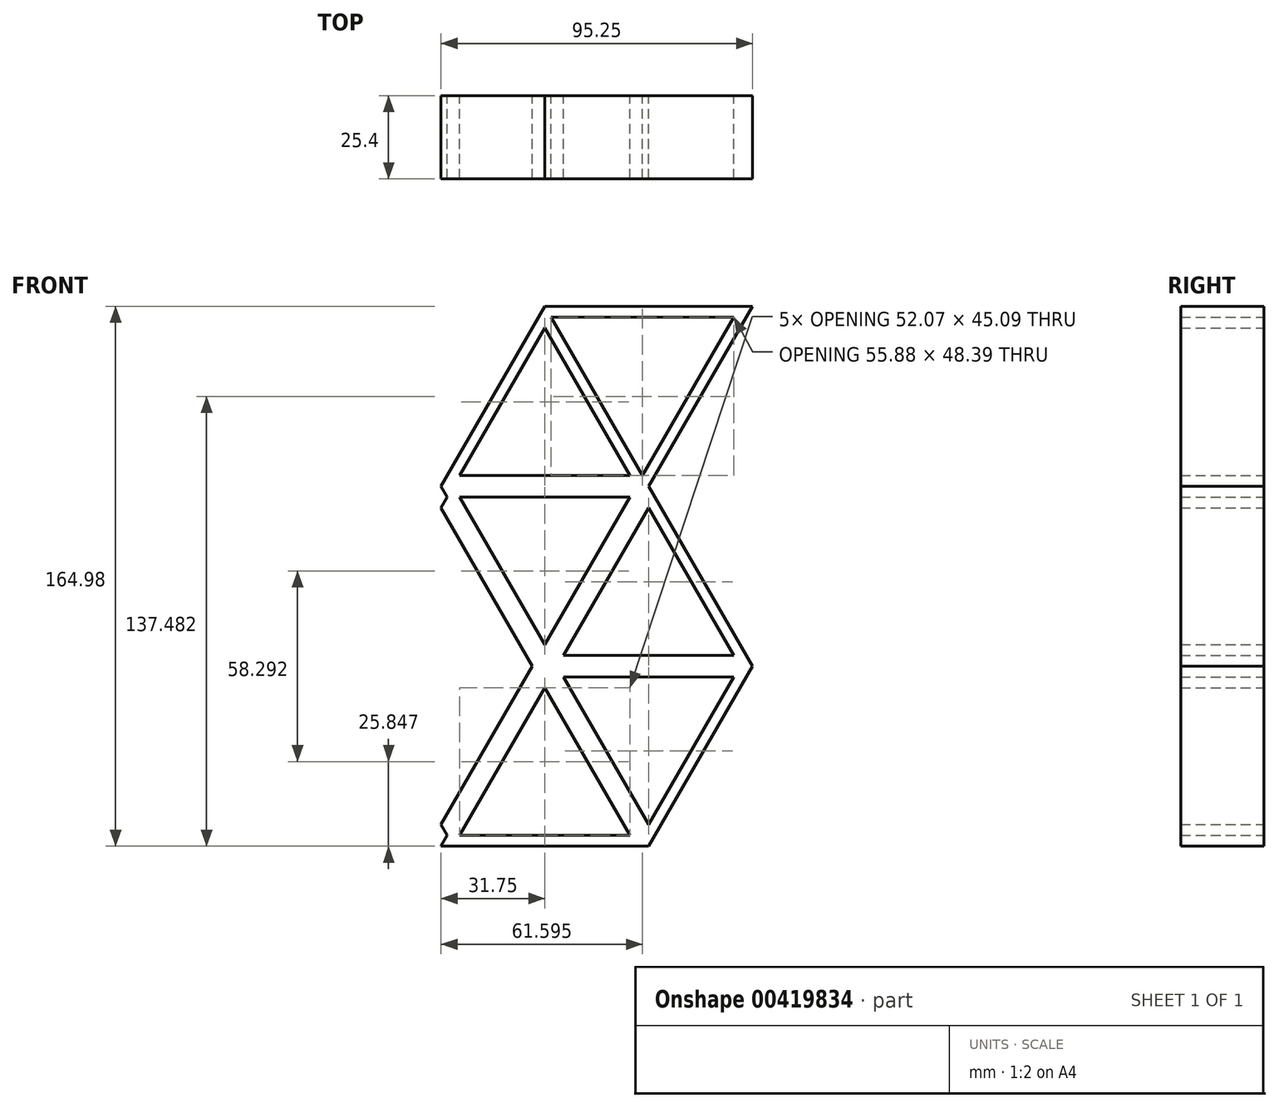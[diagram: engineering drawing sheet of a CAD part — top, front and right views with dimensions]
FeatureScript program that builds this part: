
annotation { "Feature Type Name" : "Feature", "Feature Type Description" : "" }
export const myFeature = defineFeature(function(context is Context, id is Id, definition is map)
    precondition{}
    {
        {
            var Q0;
            Q0=qCreatedBy(makeId("Front.planeOp"),FACE);
            var sketch = newSketch(context, id + "F0", { "sketchPlane" : qUnion([Q0])});
            skLineSegment(sketch, "E0", {"start": v(0, 0) * mm, "end": v(63.5, 0) * mm});
            skLineSegment(sketch, "E1", {"start": v(63.5, 0) * mm, "end": v(95.25, 55) * mm});
            skLineSegment(sketch, "E2", {"start": v(95.25, 55) * mm, "end": v(63.5, 109.99) * mm});
            skLineSegment(sketch, "E3", {"start": v(63.5, 109.99) * mm, "end": v(0, 109.99) * mm});
            skLineSegment(sketch, "E4", {"start": v(0, 109.99) * mm, "end": v(-31.75, 55) * mm});
            skLineSegment(sketch, "E5", {"start": v(-31.75, 55) * mm, "end": v(0, 0) * mm});
            skLineSegment(sketch, "E6", {"start": v(-31.75, 55) * mm, "end": v(95.25, 55) * mm});
            skLineSegment(sketch, "E7", {"start": v(63.5, 0) * mm, "end": v(0, 109.99) * mm});
            skLineSegment(sketch, "E8", {"start": v(0, 0) * mm, "end": v(63.5, 109.99) * mm});
            skLineSegment(sketch, "E9", {"start": v(63.5, 109.99) * mm, "end": v(95.25, 164.98) * mm});
            skLineSegment(sketch, "E10", {"start": v(0, 109.99) * mm, "end": v(-31.75, 164.98) * mm});
            skLineSegment(sketch, "E11", {"start": v(-31.75, 164.98) * mm, "end": v(95.25, 164.98) * mm});
            skLineSegment(sketch, "E12", {"start": v(1.9, 3.3) * mm, "end": v(61.6, 3.3) * mm});
            skLineSegment(sketch, "E13", {"start": v(61.6, 3.3) * mm, "end": v(91.44, 55) * mm});
            skLineSegment(sketch, "E14", {"start": v(91.44, 55) * mm, "end": v(61.6, 106.69) * mm});
            skLineSegment(sketch, "E15", {"start": v(61.6, 106.69) * mm, "end": v(1.9, 106.69) * mm});
            skLineSegment(sketch, "E16", {"start": v(1.9, 106.69) * mm, "end": v(-27.94, 55) * mm});
            skLineSegment(sketch, "E17", {"start": v(-27.94, 55) * mm, "end": v(1.9, 3.3) * mm});
            skLineSegment(sketch, "E18", {"start": v(5.72, 3.3) * mm, "end": v(63.5, 103.39) * mm});
            skLineSegment(sketch, "E19", {"start": v(57.78, 3.3) * mm, "end": v(0, 103.39) * mm});
            skLineSegment(sketch, "E20", {"start": v(63.5, 6.6) * mm, "end": v(5.72, 106.69) * mm});
            skLineSegment(sketch, "E21", {"start": v(89.53, 51.7) * mm, "end": v(-26.03, 51.7) * mm});
            skLineSegment(sketch, "E22", {"start": v(89.53, 58.3) * mm, "end": v(-26.03, 58.3) * mm});
            skLineSegment(sketch, "E23", {"start": v(57.78, 106.69) * mm, "end": v(0, 6.6) * mm});
            skLineSegment(sketch, "E24", {"start": v(0, 109.99) * mm, "end": v(31.75, 164.98) * mm});
            skLineSegment(sketch, "E25", {"start": v(31.75, 164.98) * mm, "end": v(63.5, 109.99) * mm});
            skLineSegment(sketch, "E26", {"start": v(-27.94, 164.98) * mm, "end": v(1.9, 113.28) * mm});
            skLineSegment(sketch, "E27", {"start": v(1.9, 113.28) * mm, "end": v(61.6, 113.28) * mm});
            skLineSegment(sketch, "E28", {"start": v(61.6, 113.28) * mm, "end": v(91.44, 164.98) * mm});
            skLineSegment(sketch, "E29", {"start": v(-29.84, 161.68) * mm, "end": v(93.34, 161.68) * mm});
            skLineSegment(sketch, "E30", {"start": v(5.71, 113.28) * mm, "end": v(35.56, 164.98) * mm});
            skLineSegment(sketch, "E31", {"start": v(57.79, 113.28) * mm, "end": v(27.94, 164.98) * mm});
            skSolve(sketch);
        }
        {
            var Q0;
            {var subQ0=sQuery(id+"F0.wireOp",EDGE,"E28");var subQ1=sQuery(id+"F0.wireOp",EDGE,"E11");var subQ2=makeQuery(id+"F0.imprint","INTERSECT",VERTEX,{"derivedFrom":[subQ1,subQ0]});Q0=makeQuery(id+"F0.imprint","IMPRINT",FACE,{"disambiguationData":[TD([[makeQuery(id+"F0.imprint","IMPRINT",EDGE,{"disambiguationData":[TD([[subQ2,1.0]])],"derivedFrom":subQ1}),-1.0]])]});}
            var Q1;
            {var subQ0=sQuery(id+"F0.wireOp",EDGE,"E11");var subQ1=sQuery(id+"F0.wireOp",EDGE,"E9");var subQ2=makeQuery(id+"F0.imprint","INTERSECT",VERTEX,{"derivedFrom":[subQ1,subQ0]});Q1=makeQuery(id+"F0.imprint","IMPRINT",FACE,{"disambiguationData":[TD([[makeQuery(id+"F0.imprint","IMPRINT",EDGE,{"disambiguationData":[TD([[subQ2,1.0]])],"derivedFrom":subQ1}),1.0]])]});}
            var Q2;
            {var subQ1=sQuery(id+"F0.wireOp",EDGE,"E9");var subQ3=sQuery(id+"F0.wireOp",EDGE,"E29");var subQ4=makeQuery(id+"F0.imprint","INTERSECT",VERTEX,{"derivedFrom":[subQ1,subQ3]});Q2=makeQuery(id+"F0.imprint","IMPRINT",FACE,{"disambiguationData":[TD([[makeQuery(id+"F0.imprint","IMPRINT",EDGE,{"disambiguationData":[TD([[subQ4,1.0]])],"derivedFrom":subQ3}),-1.0]])]});}
            var Q3;
            {var subQ1=sQuery(id+"F0.wireOp",EDGE,"E11");var subQ3=sQuery(id+"F0.wireOp",EDGE,"E30");var subQ4=makeQuery(id+"F0.imprint","INTERSECT",VERTEX,{"derivedFrom":[subQ1,subQ3]});Q3=makeQuery(id+"F0.imprint","IMPRINT",FACE,{"disambiguationData":[TD([[makeQuery(id+"F0.imprint","IMPRINT",EDGE,{"disambiguationData":[TD([[subQ4,1.0]])],"derivedFrom":subQ1}),-1.0]])]});}
            var Q4;
            {var subQ0=sQuery(id+"F0.wireOp",EDGE,"E31");var subQ3=sQuery(id+"F0.wireOp",EDGE,"E30");var subQ5=makeQuery(id+"F0.imprint","INTERSECT",VERTEX,{"derivedFrom":[subQ3,subQ0]});Q4=makeQuery(id+"F0.imprint","IMPRINT",FACE,{"disambiguationData":[TD([[makeQuery(id+"F0.imprint","IMPRINT",EDGE,{"disambiguationData":[TD([[subQ5,-1.0]])],"derivedFrom":subQ3}),1.0]])]});}
            var Q5;
            {var subQ0=sQuery(id+"F0.wireOp",EDGE,"E25");var subQ1=sQuery(id+"F0.wireOp",EDGE,"E24");var subQ2=makeQuery(id+"F0.imprint","INTERSECT",VERTEX,{"derivedFrom":[sQuery(id+"F0.wireOp",EDGE,"E11"),subQ1,subQ0]});Q5=makeQuery(id+"F0.imprint","IMPRINT",FACE,{"disambiguationData":[TD([[makeQuery(id+"F0.imprint","IMPRINT",EDGE,{"disambiguationData":[TD([[subQ2,1.0]])],"derivedFrom":subQ1}),-1.0]])]});}
            var Q6;
            {var subQ0=sQuery(id+"F0.wireOp",EDGE,"E27");var subQ5=sQuery(id+"F0.wireOp",EDGE,"E31");var subQ7=makeQuery(id+"F0.imprint","INTERSECT",VERTEX,{"derivedFrom":[subQ0,subQ5]});Q6=makeQuery(id+"F0.imprint","IMPRINT",FACE,{"disambiguationData":[TD([[makeQuery(id+"F0.imprint","IMPRINT",EDGE,{"disambiguationData":[TD([[subQ7,-1.0]])],"derivedFrom":subQ5}),-1.0]])]});}
            var Q7;
            {var subQ0=sQuery(id+"F0.wireOp",EDGE,"E27");var subQ5=sQuery(id+"F0.wireOp",EDGE,"E30");var subQ6=makeQuery(id+"F0.imprint","INTERSECT",VERTEX,{"derivedFrom":[subQ0,subQ5]});Q7=makeQuery(id+"F0.imprint","IMPRINT",FACE,{"disambiguationData":[TD([[makeQuery(id+"F0.imprint","IMPRINT",EDGE,{"disambiguationData":[TD([[subQ6,-1.0]])],"derivedFrom":subQ5}),1.0]])]});}
            var Q8;
            {var subQ5=sQuery(id+"F0.wireOp",EDGE,"E3");Q8=makeQuery(id+"F0.imprint","IMPRINT",FACE,{"disambiguationData":[TD([[makeQuery(id+"F0.imprint","IMPRINT",EDGE,{"derivedFrom":subQ5}),-1.0]])]});}
            var Q9;
            {var subQ1=sQuery(id+"F0.wireOp",EDGE,"E3");Q9=makeQuery(id+"F0.imprint","IMPRINT",FACE,{"disambiguationData":[TD([[makeQuery(id+"F0.imprint","IMPRINT",EDGE,{"derivedFrom":subQ1}),1.0]])]});}
            var Q10;
            {var subQ0=sQuery(id+"F0.wireOp",EDGE,"E15");var subQ5=sQuery(id+"F0.wireOp",EDGE,"E20");var subQ6=makeQuery(id+"F0.imprint","INTERSECT",VERTEX,{"derivedFrom":[subQ0,subQ5]});Q10=makeQuery(id+"F0.imprint","IMPRINT",FACE,{"disambiguationData":[TD([[makeQuery(id+"F0.imprint","IMPRINT",EDGE,{"disambiguationData":[TD([[subQ6,1.0]])],"derivedFrom":subQ5}),1.0]])]});}
            var Q11;
            {var subQ0=sQuery(id+"F0.wireOp",EDGE,"E15");var subQ5=sQuery(id+"F0.wireOp",EDGE,"E23");var subQ6=makeQuery(id+"F0.imprint","INTERSECT",VERTEX,{"derivedFrom":[subQ0,subQ5]});Q11=makeQuery(id+"F0.imprint","IMPRINT",FACE,{"disambiguationData":[TD([[makeQuery(id+"F0.imprint","IMPRINT",EDGE,{"disambiguationData":[TD([[subQ6,-1.0]])],"derivedFrom":subQ5}),1.0]])]});}
            var Q12;
            {var subQ0=sQuery(id+"F0.wireOp",EDGE,"E23");var subQ1=sQuery(id+"F0.wireOp",EDGE,"E20");var subQ2=makeQuery(id+"F0.imprint","INTERSECT",VERTEX,{"derivedFrom":[subQ1,subQ0]});Q12=makeQuery(id+"F0.imprint","IMPRINT",FACE,{"disambiguationData":[TD([[makeQuery(id+"F0.imprint","IMPRINT",EDGE,{"disambiguationData":[TD([[subQ2,1.0]])],"derivedFrom":subQ1}),1.0]])]});}
            var Q13;
            {var subQ0=sQuery(id+"F0.wireOp",EDGE,"E8");var subQ1=sQuery(id+"F0.wireOp",EDGE,"E6");var subQ2=makeQuery(id+"F0.imprint","INTERSECT",VERTEX,{"derivedFrom":[subQ1,sQuery(id+"F0.wireOp",EDGE,"E7"),subQ0]});Q13=makeQuery(id+"F0.imprint","IMPRINT",FACE,{"disambiguationData":[TD([[makeQuery(id+"F0.imprint","IMPRINT",EDGE,{"disambiguationData":[TD([[subQ2,-1.0]])],"derivedFrom":subQ1}),1.0]])]});}
            var Q14;
            {var subQ0=sQuery(id+"F0.wireOp",EDGE,"E8");var subQ1=sQuery(id+"F0.wireOp",EDGE,"E7");var subQ2=makeQuery(id+"F0.imprint","INTERSECT",VERTEX,{"derivedFrom":[sQuery(id+"F0.wireOp",EDGE,"E6"),subQ1,subQ0]});Q14=makeQuery(id+"F0.imprint","IMPRINT",FACE,{"disambiguationData":[TD([[makeQuery(id+"F0.imprint","IMPRINT",EDGE,{"disambiguationData":[TD([[subQ2,-1.0]])],"derivedFrom":subQ1}),-1.0]])]});}
            var Q15;
            {var subQ0=sQuery(id+"F0.wireOp",EDGE,"E14");var subQ5=sQuery(id+"F0.wireOp",EDGE,"E18");var subQ6=makeQuery(id+"F0.imprint","INTERSECT",VERTEX,{"derivedFrom":[subQ0,subQ5]});Q15=makeQuery(id+"F0.imprint","IMPRINT",FACE,{"disambiguationData":[TD([[makeQuery(id+"F0.imprint","IMPRINT",EDGE,{"disambiguationData":[TD([[subQ6,1.0]])],"derivedFrom":subQ5}),1.0]])]});}
            var Q16;
            {var subQ5=sQuery(id+"F0.wireOp",EDGE,"E2");Q16=makeQuery(id+"F0.imprint","IMPRINT",FACE,{"disambiguationData":[TD([[makeQuery(id+"F0.imprint","IMPRINT",EDGE,{"derivedFrom":subQ5}),1.0]])]});}
            var Q17;
            {var subQ0=sQuery(id+"F0.wireOp",EDGE,"E13");var subQ5=sQuery(id+"F0.wireOp",EDGE,"E21");var subQ6=makeQuery(id+"F0.imprint","INTERSECT",VERTEX,{"derivedFrom":[subQ0,subQ5]});Q17=makeQuery(id+"F0.imprint","IMPRINT",FACE,{"disambiguationData":[TD([[makeQuery(id+"F0.imprint","IMPRINT",EDGE,{"disambiguationData":[TD([[subQ6,-1.0]])],"derivedFrom":subQ5}),-1.0]])]});}
            var Q18;
            {var subQ4=sQuery(id+"F0.wireOp",EDGE,"E1");Q18=makeQuery(id+"F0.imprint","IMPRINT",FACE,{"disambiguationData":[TD([[makeQuery(id+"F0.imprint","IMPRINT",EDGE,{"derivedFrom":subQ4}),1.0]])]});}
            var Q19;
            {var subQ5=sQuery(id+"F0.wireOp",EDGE,"E0");Q19=makeQuery(id+"F0.imprint","IMPRINT",FACE,{"disambiguationData":[TD([[makeQuery(id+"F0.imprint","IMPRINT",EDGE,{"derivedFrom":subQ5}),1.0]])]});}
            var Q20;
            {var subQ0=sQuery(id+"F0.wireOp",EDGE,"E12");var subQ5=sQuery(id+"F0.wireOp",EDGE,"E18");var subQ6=makeQuery(id+"F0.imprint","INTERSECT",VERTEX,{"derivedFrom":[subQ0,subQ5]});Q20=makeQuery(id+"F0.imprint","IMPRINT",FACE,{"disambiguationData":[TD([[makeQuery(id+"F0.imprint","IMPRINT",EDGE,{"disambiguationData":[TD([[subQ6,-1.0]])],"derivedFrom":subQ5}),1.0]])]});}
            var Q21;
            {var subQ0=sQuery(id+"F0.wireOp",EDGE,"E19");var subQ1=sQuery(id+"F0.wireOp",EDGE,"E18");var subQ2=makeQuery(id+"F0.imprint","INTERSECT",VERTEX,{"derivedFrom":[subQ1,subQ0]});Q21=makeQuery(id+"F0.imprint","IMPRINT",FACE,{"disambiguationData":[TD([[makeQuery(id+"F0.imprint","IMPRINT",EDGE,{"disambiguationData":[TD([[subQ2,-1.0]])],"derivedFrom":subQ1}),1.0]])]});}
            var Q22;
            {var subQ0=sQuery(id+"F0.wireOp",EDGE,"E8");var subQ1=sQuery(id+"F0.wireOp",EDGE,"E7");var subQ2=makeQuery(id+"F0.imprint","INTERSECT",VERTEX,{"derivedFrom":[sQuery(id+"F0.wireOp",EDGE,"E6"),subQ1,subQ0]});Q22=makeQuery(id+"F0.imprint","IMPRINT",FACE,{"disambiguationData":[TD([[makeQuery(id+"F0.imprint","IMPRINT",EDGE,{"disambiguationData":[TD([[subQ2,1.0]])],"derivedFrom":subQ1}),1.0]])]});}
            var Q23;
            {var subQ0=sQuery(id+"F0.wireOp",EDGE,"E7");var subQ1=sQuery(id+"F0.wireOp",EDGE,"E6");var subQ2=makeQuery(id+"F0.imprint","INTERSECT",VERTEX,{"derivedFrom":[subQ1,subQ0,sQuery(id+"F0.wireOp",EDGE,"E8")]});Q23=makeQuery(id+"F0.imprint","IMPRINT",FACE,{"disambiguationData":[TD([[makeQuery(id+"F0.imprint","IMPRINT",EDGE,{"disambiguationData":[TD([[subQ2,-1.0]])],"derivedFrom":subQ1}),-1.0]])]});}
            var Q24;
            {var subQ0=sQuery(id+"F0.wireOp",EDGE,"E13");var subQ5=sQuery(id+"F0.wireOp",EDGE,"E20");var subQ7=makeQuery(id+"F0.imprint","INTERSECT",VERTEX,{"derivedFrom":[subQ0,subQ5]});Q24=makeQuery(id+"F0.imprint","IMPRINT",FACE,{"disambiguationData":[TD([[makeQuery(id+"F0.imprint","IMPRINT",EDGE,{"disambiguationData":[TD([[subQ7,-1.0]])],"derivedFrom":subQ5}),1.0]])]});}
            var Q25;
            {var subQ0=sQuery(id+"F0.wireOp",EDGE,"E12");var subQ5=sQuery(id+"F0.wireOp",EDGE,"E19");var subQ7=makeQuery(id+"F0.imprint","INTERSECT",VERTEX,{"derivedFrom":[subQ0,subQ5]});Q25=makeQuery(id+"F0.imprint","IMPRINT",FACE,{"disambiguationData":[TD([[makeQuery(id+"F0.imprint","IMPRINT",EDGE,{"disambiguationData":[TD([[subQ7,-1.0]])],"derivedFrom":subQ5}),-1.0]])]});}
            var Q26;
            {var subQ0=sQuery(id+"F0.wireOp",EDGE,"E20");var subQ3=sQuery(id+"F0.wireOp",EDGE,"E21");var subQ5=makeQuery(id+"F0.imprint","INTERSECT",VERTEX,{"derivedFrom":[subQ0,subQ3]});Q26=makeQuery(id+"F0.imprint","IMPRINT",FACE,{"disambiguationData":[TD([[makeQuery(id+"F0.imprint","IMPRINT",EDGE,{"disambiguationData":[TD([[subQ5,-1.0]])],"derivedFrom":subQ0}),1.0]])]});}
            var Q27;
            {var subQ0=sQuery(id+"F0.wireOp",EDGE,"E14");var subQ5=sQuery(id+"F0.wireOp",EDGE,"E22");var subQ6=makeQuery(id+"F0.imprint","INTERSECT",VERTEX,{"derivedFrom":[subQ0,subQ5]});Q27=makeQuery(id+"F0.imprint","IMPRINT",FACE,{"disambiguationData":[TD([[makeQuery(id+"F0.imprint","IMPRINT",EDGE,{"disambiguationData":[TD([[subQ6,-1.0]])],"derivedFrom":subQ5}),1.0]])]});}
            var Q28;
            {var subQ0=sQuery(id+"F0.wireOp",EDGE,"E22");var subQ1=sQuery(id+"F0.wireOp",EDGE,"E18");var subQ2=makeQuery(id+"F0.imprint","INTERSECT",VERTEX,{"derivedFrom":[subQ1,subQ0]});Q28=makeQuery(id+"F0.imprint","IMPRINT",FACE,{"disambiguationData":[TD([[makeQuery(id+"F0.imprint","IMPRINT",EDGE,{"disambiguationData":[TD([[subQ2,1.0]])],"derivedFrom":subQ1}),1.0]])]});}
            var Q29;
            {var subQ0=sQuery(id+"F0.wireOp",EDGE,"E17");var subQ5=sQuery(id+"F0.wireOp",EDGE,"E23");var subQ6=makeQuery(id+"F0.imprint","INTERSECT",VERTEX,{"derivedFrom":[subQ0,subQ5]});Q29=makeQuery(id+"F0.imprint","IMPRINT",FACE,{"disambiguationData":[TD([[makeQuery(id+"F0.imprint","IMPRINT",EDGE,{"disambiguationData":[TD([[subQ6,1.0]])],"derivedFrom":subQ5}),1.0]])]});}
            var Q30;
            {var subQ0=sQuery(id+"F0.wireOp",EDGE,"E23");var subQ3=sQuery(id+"F0.wireOp",EDGE,"E21");var subQ5=makeQuery(id+"F0.imprint","INTERSECT",VERTEX,{"derivedFrom":[subQ3,subQ0]});Q30=makeQuery(id+"F0.imprint","IMPRINT",FACE,{"disambiguationData":[TD([[makeQuery(id+"F0.imprint","IMPRINT",EDGE,{"disambiguationData":[TD([[subQ5,1.0]])],"derivedFrom":subQ3}),-1.0]])]});}
            var Q31;
            {var subQ0=sQuery(id+"F0.wireOp",EDGE,"E19");var subQ1=sQuery(id+"F0.wireOp",EDGE,"E6");var subQ2=makeQuery(id+"F0.imprint","INTERSECT",VERTEX,{"derivedFrom":[subQ1,subQ0,sQuery(id+"F0.wireOp",EDGE,"E23")]});Q31=makeQuery(id+"F0.imprint","IMPRINT",FACE,{"disambiguationData":[TD([[makeQuery(id+"F0.imprint","IMPRINT",EDGE,{"disambiguationData":[TD([[subQ2,-1.0]])],"derivedFrom":subQ1}),-1.0]])]});}
            var Q32;
            {var subQ0=sQuery(id+"F0.wireOp",EDGE,"E23");var subQ1=sQuery(id+"F0.wireOp",EDGE,"E6");var subQ2=makeQuery(id+"F0.imprint","INTERSECT",VERTEX,{"derivedFrom":[subQ1,sQuery(id+"F0.wireOp",EDGE,"E19"),subQ0]});Q32=makeQuery(id+"F0.imprint","IMPRINT",FACE,{"disambiguationData":[TD([[makeQuery(id+"F0.imprint","IMPRINT",EDGE,{"disambiguationData":[TD([[subQ2,-1.0]])],"derivedFrom":subQ1}),1.0]])]});}
            var Q33;
            {var subQ0=sQuery(id+"F0.wireOp",EDGE,"E22");var subQ1=sQuery(id+"F0.wireOp",EDGE,"E19");var subQ2=makeQuery(id+"F0.imprint","INTERSECT",VERTEX,{"derivedFrom":[subQ1,subQ0]});Q33=makeQuery(id+"F0.imprint","IMPRINT",FACE,{"disambiguationData":[TD([[makeQuery(id+"F0.imprint","IMPRINT",EDGE,{"disambiguationData":[TD([[subQ2,1.0]])],"derivedFrom":subQ1}),-1.0]])]});}
            var Q34;
            {var subQ0=sQuery(id+"F0.wireOp",EDGE,"E16");var subQ5=sQuery(id+"F0.wireOp",EDGE,"E19");var subQ6=makeQuery(id+"F0.imprint","INTERSECT",VERTEX,{"derivedFrom":[subQ0,subQ5]});Q34=makeQuery(id+"F0.imprint","IMPRINT",FACE,{"disambiguationData":[TD([[makeQuery(id+"F0.imprint","IMPRINT",EDGE,{"disambiguationData":[TD([[subQ6,1.0]])],"derivedFrom":subQ5}),-1.0]])]});}
            extrude(context, id + "F1", {"entities" : qUnion([Q0, Q1, Q2, Q3, Q4, Q5, Q6, Q7, Q8, Q9, Q10, Q11, Q12, Q13, Q14, Q15, Q16, Q17, Q18, Q19, Q20, Q21, Q22, Q23, Q24, Q25, Q26, Q27, Q28, Q29, Q30, Q31, Q32, Q33, Q34]), "depth" : 25.4 * mm});
        }
    });
